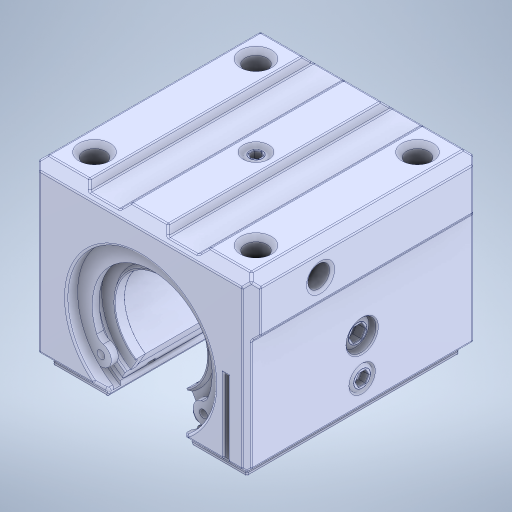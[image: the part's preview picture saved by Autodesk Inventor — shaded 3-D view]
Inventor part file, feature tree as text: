
AUTODESK INVENTOR PART (.ipt)
format: ipt  version: 2024 (Build 280153000, 153)  size: 1,103,360 bytes
history: native  units: in
note: dims shown in document units (in); Inventor stores cm internally (conversion verified against a paired STEP export)
features: other x12, extrude x1, sketch x1
ambient origin geometry x8: Origin, YZ Plane, XZ Plane, XY Plane, X Axis, Y Axis, Z Axis, Center Point
bodies: Solid1 (feature_tree), Solid2 (feature_tree), Solid3 (feature_tree), Solid4 (feature_tree), Solid5 (feature_tree), Solid6 (feature_tree), Solid7 (feature_tree), Solid8 (feature_tree), Solid9 (feature_tree), Solid10 (feature_tree), Solid11 (feature_tree), Solid12 (feature_tree)
feature tree (14):
  extrude  "Extrusion1"  Depth=3.937in TaperAngle=0.0deg
  sketch  "Sketch1"  dims[d0=1.2638in d1=3.937in d2=0.0in]
  other  "Корпус SBR20UU_1:1"
  other  "Корпус SBR20UU_1:2"
  other  "Корпус SBR20UU_1:3"
  other  "Подшипник LM20UUOP_2:1"
  other  "Подшипник LM20UUOP_2:2"
  other  "Подшипник LM20UUOP_2:3"
  other  "Подшипник LM20UUOP_2:4"
  other  "Стопорный винт М4х6_3:1"
  other  "Стопорный винт М6х6_4:1"
  other  "Стопорное кольцо_5:1"
  other  "Стопорное кольцо_6:1"
  other  "Стопорный винт М5х5_7:1"
